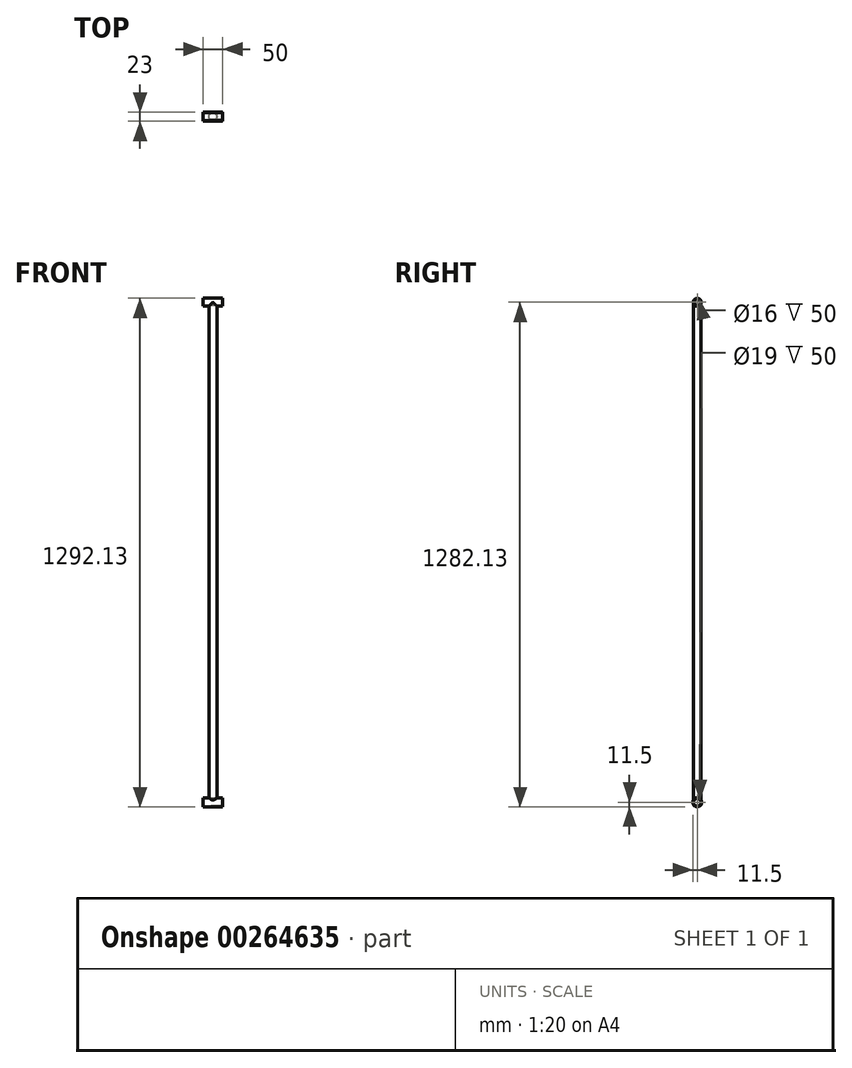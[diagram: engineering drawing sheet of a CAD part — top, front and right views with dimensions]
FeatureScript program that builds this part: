
annotation { "Feature Type Name" : "Feature", "Feature Type Description" : "" }
export const myFeature = defineFeature(function(context is Context, id is Id, definition is map)
    precondition{}
    {
        {
            var Q0;
            Q0=qCreatedBy(makeId("Front.planeOp"),FACE);
            var sketch = newSketch(context, id + "F0", { "sketchPlane" : qUnion([Q0])});
            skLineSegment(sketch, "E0", {"start": v(0, 0) * mm, "end": v(50, 0) * mm});
            skLineSegment(sketch, "E1", {"start": v(50, 23) * mm, "end": v(35, 23) * mm});
            skLineSegment(sketch, "E2", {"start": v(35, 23) * mm, "end": v(35, 1272.13) * mm});
            skLineSegment(sketch, "E3", {"start": v(35, 1272.13) * mm, "end": v(50, 1272.13) * mm});
            skLineSegment(sketch, "E4", {"start": v(50, 1292.13) * mm, "end": v(0, 1292.13) * mm});
            skLineSegment(sketch, "E5", {"start": v(0, 1272.13) * mm, "end": v(15, 1272.13) * mm});
            skLineSegment(sketch, "E6", {"start": v(15, 1272.13) * mm, "end": v(15, 23) * mm});
            skLineSegment(sketch, "E7", {"start": v(15, 23) * mm, "end": v(0, 23) * mm});
            skLineSegment(sketch, "E8", {"start": v(15, 23) * mm, "end": v(35, 23) * mm});
            skLineSegment(sketch, "E9", {"start": v(15, 1272.13) * mm, "end": v(35, 1272.13) * mm});
            skLineSegment(sketch, "E10", {"start": v(0, 1272.13) * mm, "end": v(0, 1274.13) * mm});
            skLineSegment(sketch, "E11", {"start": v(0, 1274.13) * mm, "end": v(0, 1290.13) * mm});
            skLineSegment(sketch, "E12", {"start": v(0, 1290.13) * mm, "end": v(0, 1292.13) * mm});
            skLineSegment(sketch, "E13", {"start": v(0, 1274.13) * mm, "end": v(50, 1274.13) * mm});
            skLineSegment(sketch, "E14", {"start": v(50, 1274.13) * mm, "end": v(50, 1272.13) * mm});
            skLineSegment(sketch, "E15", {"start": v(50, 1274.13) * mm, "end": v(50, 1290.13) * mm});
            skLineSegment(sketch, "E16", {"start": v(50, 1290.13) * mm, "end": v(50, 1292.13) * mm});
            skLineSegment(sketch, "E17", {"start": v(50, 1290.13) * mm, "end": v(0, 1290.13) * mm});
            skLineSegment(sketch, "E18", {"start": v(0, 0) * mm, "end": v(0, 2) * mm});
            skLineSegment(sketch, "E19", {"start": v(0, 2) * mm, "end": v(0, 21) * mm});
            skLineSegment(sketch, "E20", {"start": v(0, 21) * mm, "end": v(0, 23) * mm});
            skLineSegment(sketch, "E21", {"start": v(0, 21) * mm, "end": v(50, 21) * mm});
            skLineSegment(sketch, "E22", {"start": v(50, 21) * mm, "end": v(50, 23) * mm});
            skLineSegment(sketch, "E23", {"start": v(50, 21) * mm, "end": v(50, 2) * mm});
            skLineSegment(sketch, "E24", {"start": v(50, 2) * mm, "end": v(0, 2) * mm});
            skLineSegment(sketch, "E25", {"start": v(50, 2) * mm, "end": v(50, 0) * mm});
            skSolve(sketch);
        }
        {
            var Q0;
            Q0=makeQuery(id+"F0.imprint","IMPRINT",FACE,{"disambiguationData":[TD([[makeQuery(id+"F0.imprint","IMPRINT",EDGE,{"derivedFrom":sQuery(id+"F0.wireOp",EDGE,"E2")}),1.0]])]});
            var Q1;
            Q1=makeQuery(id+"F0.imprint","IMPRINT",FACE,{"disambiguationData":[TD([[makeQuery(id+"F0.imprint","IMPRINT",EDGE,{"derivedFrom":sQuery(id+"F0.wireOp",EDGE,"E3")}),1.0]])]});
            var Q2;
            Q2=makeQuery(id+"F0.imprint","IMPRINT",FACE,{"disambiguationData":[TD([[makeQuery(id+"F0.imprint","IMPRINT",EDGE,{"derivedFrom":sQuery(id+"F0.wireOp",EDGE,"E11")}),-1.0]])]});
            var Q3;
            Q3=makeQuery(id+"F0.imprint","IMPRINT",FACE,{"disambiguationData":[TD([[makeQuery(id+"F0.imprint","IMPRINT",EDGE,{"derivedFrom":sQuery(id+"F0.wireOp",EDGE,"E4")}),1.0]])]});
            extrude(context, id + "F1", {"entities" : qUnion([Q0, Q1, Q2, Q3]), "endBound" : BoundingType.SYMMETRIC, "depth" : 20 * mm});
        }
        {
            var Q0;
            Q0=makeQuery(id+"F0.imprint","IMPRINT",FACE,{"disambiguationData":[TD([[makeQuery(id+"F0.imprint","IMPRINT",EDGE,{"derivedFrom":sQuery(id+"F0.wireOp",EDGE,"E1")}),1.0]])]});
            var Q1;
            Q1=makeQuery(id+"F0.imprint","IMPRINT",FACE,{"disambiguationData":[TD([[makeQuery(id+"F0.imprint","IMPRINT",EDGE,{"derivedFrom":sQuery(id+"F0.wireOp",EDGE,"E19")}),-1.0]])]});
            var Q2;
            Q2=makeQuery(id+"F0.imprint","IMPRINT",FACE,{"disambiguationData":[TD([[makeQuery(id+"F0.imprint","IMPRINT",EDGE,{"derivedFrom":sQuery(id+"F0.wireOp",EDGE,"E0")}),1.0]])]});
            extrude(context, id + "F2", {"entities" : qUnion([Q0, Q1, Q2]), "operationType" : NewBodyOperationType.ADD, "endBound" : BoundingType.SYMMETRIC, "depth" : 23 * mm});
        }
        {
            var Q0;
            Q0=makeQuery(id+"F0.imprint","IMPRINT",FACE,{"disambiguationData":[TD([[makeQuery(id+"F0.imprint","IMPRINT",EDGE,{"derivedFrom":sQuery(id+"F0.wireOp",EDGE,"E19")}),-1.0]])]});
            extrude(context, id + "F3", {"entities" : qUnion([Q0]), "operationType" : NewBodyOperationType.REMOVE, "endBound" : BoundingType.SYMMETRIC, "oppositeDirection" : true, "depth" : 19 * mm});
        }
        {
            var Q0;
            Q0=makeQuery(id+"F0.imprint","IMPRINT",FACE,{"disambiguationData":[TD([[makeQuery(id+"F0.imprint","IMPRINT",EDGE,{"derivedFrom":sQuery(id+"F0.wireOp",EDGE,"E11")}),-1.0]])]});
            extrude(context, id + "F4", {"entities" : qUnion([Q0]), "operationType" : NewBodyOperationType.REMOVE, "endBound" : BoundingType.SYMMETRIC, "oppositeDirection" : true, "depth" : 16 * mm});
        }
        {
            var Q0;
            Q0=makeQuery(id+"F4.boolean.opBoolean","COPY",EDGE,{"derivedFrom":makeQuery(id+"F4.opExtrude","CAP_EDGE",EDGE,{"disambiguationData":[OSD([sQuery(id+"F0.wireOp",EDGE,"E17")])],"isStart":true})});
            var Q1;
            Q1=makeQuery(id+"F4.boolean.opBoolean","COPY",EDGE,{"derivedFrom":makeQuery(id+"F4.opExtrude","CAP_EDGE",EDGE,{"disambiguationData":[OSD([sQuery(id+"F0.wireOp",EDGE,"E13")])],"isStart":true})});
            var Q2;
            Q2=makeQuery(id+"F4.boolean.opBoolean","COPY",EDGE,{"derivedFrom":makeQuery(id+"F4.opExtrude","CAP_EDGE",EDGE,{"disambiguationData":[OSD([sQuery(id+"F0.wireOp",EDGE,"E13")])],"isStart":false})});
            var Q3;
            Q3=makeQuery(id+"F4.boolean.opBoolean","COPY",EDGE,{"derivedFrom":makeQuery(id+"F4.opExtrude","CAP_EDGE",EDGE,{"disambiguationData":[OSD([sQuery(id+"F0.wireOp",EDGE,"E17")])],"isStart":false})});
            fillet(context, id + "F5", {"entities" : qUnion([Q0, Q1, Q2, Q3]), "radius" : 8 * mm, "tangentPropagation" : true, "allowEdgeOverflow" : false});
        }
        {
            var Q0;
            Q0=makeQuery(id+"F3.boolean.opBoolean","COPY",EDGE,{"derivedFrom":makeQuery(id+"F3.opExtrude","CAP_EDGE",EDGE,{"disambiguationData":[OSD([sQuery(id+"F0.wireOp",EDGE,"E24")])],"isStart":false})});
            var Q1;
            Q1=makeQuery(id+"F3.boolean.opBoolean","COPY",EDGE,{"derivedFrom":makeQuery(id+"F3.opExtrude","CAP_EDGE",EDGE,{"disambiguationData":[OSD([sQuery(id+"F0.wireOp",EDGE,"E24")])],"isStart":true})});
            var Q2;
            Q2=makeQuery(id+"F3.boolean.opBoolean","COPY",EDGE,{"derivedFrom":makeQuery(id+"F3.opExtrude","CAP_EDGE",EDGE,{"disambiguationData":[OSD([sQuery(id+"F0.wireOp",EDGE,"E21")])],"isStart":true})});
            var Q3;
            Q3=makeQuery(id+"F3.boolean.opBoolean","COPY",EDGE,{"derivedFrom":makeQuery(id+"F3.opExtrude","CAP_EDGE",EDGE,{"disambiguationData":[OSD([sQuery(id+"F0.wireOp",EDGE,"E21")])],"isStart":false})});
            fillet(context, id + "F6", {"entities" : qUnion([Q0, Q1, Q2, Q3]), "radius" : 9.5 * mm, "tangentPropagation" : true, "allowEdgeOverflow" : false});
        }
        {
            var Q0;
            Q0=makeQuery(id+"F2.opExtrude","CAP_EDGE",EDGE,{"disambiguationData":[OSD([sQuery(id+"F0.wireOp",EDGE,"E1"),sQuery(id+"F0.wireOp",EDGE,"E7"),sQuery(id+"F0.wireOp",EDGE,"E8")])],"isStart":false});
            var Q1;
            Q1=makeQuery(id+"F2.opExtrude","CAP_EDGE",EDGE,{"disambiguationData":[OSD([sQuery(id+"F0.wireOp",EDGE,"E0")])],"isStart":false});
            var Q2;
            Q2=makeQuery(id+"F2.opExtrude","CAP_EDGE",EDGE,{"disambiguationData":[OSD([sQuery(id+"F0.wireOp",EDGE,"E0")])],"isStart":true});
            var Q3;
            Q3=makeQuery(id+"F2.opExtrude","CAP_EDGE",EDGE,{"disambiguationData":[OSD([sQuery(id+"F0.wireOp",EDGE,"E1"),sQuery(id+"F0.wireOp",EDGE,"E7"),sQuery(id+"F0.wireOp",EDGE,"E8")])],"isStart":true});
            fillet(context, id + "F7", {"entities" : qUnion([Q0, Q1, Q2, Q3]), "radius" : 11.5 * mm, "tangentPropagation" : true, "allowEdgeOverflow" : false});
        }
        {
            var Q0;
            Q0=makeQuery(id+"F1.opExtrude","CAP_EDGE",EDGE,{"disambiguationData":[OSD([sQuery(id+"F0.wireOp",EDGE,"E5")])],"isStart":false});
            var Q1;
            Q1=makeQuery(id+"F1.opExtrude","CAP_EDGE",EDGE,{"disambiguationData":[OSD([sQuery(id+"F0.wireOp",EDGE,"E4")])],"isStart":false});
            var Q2;
            Q2=makeQuery(id+"F1.opExtrude","CAP_EDGE",EDGE,{"disambiguationData":[OSD([sQuery(id+"F0.wireOp",EDGE,"E3")])],"isStart":false});
            var Q3;
            Q3=makeQuery(id+"F1.opExtrude","CAP_EDGE",EDGE,{"disambiguationData":[OSD([sQuery(id+"F0.wireOp",EDGE,"E2")])],"isStart":false});
            var Q4;
            Q4=makeQuery(id+"F1.opExtrude","CAP_EDGE",EDGE,{"disambiguationData":[OSD([sQuery(id+"F0.wireOp",EDGE,"E6")])],"isStart":false});
            var Q5;
            Q5=makeQuery(id+"F1.opExtrude","CAP_EDGE",EDGE,{"disambiguationData":[OSD([sQuery(id+"F0.wireOp",EDGE,"E2")])],"isStart":true});
            var Q6;
            Q6=makeQuery(id+"F1.opExtrude","CAP_EDGE",EDGE,{"disambiguationData":[OSD([sQuery(id+"F0.wireOp",EDGE,"E3")])],"isStart":true});
            var Q7;
            Q7=makeQuery(id+"F1.opExtrude","CAP_EDGE",EDGE,{"disambiguationData":[OSD([sQuery(id+"F0.wireOp",EDGE,"E4")])],"isStart":true});
            var Q8;
            Q8=makeQuery(id+"F1.opExtrude","CAP_EDGE",EDGE,{"disambiguationData":[OSD([sQuery(id+"F0.wireOp",EDGE,"E6")])],"isStart":true});
            var Q9;
            Q9=makeQuery(id+"F1.opExtrude","CAP_EDGE",EDGE,{"disambiguationData":[OSD([sQuery(id+"F0.wireOp",EDGE,"E5")])],"isStart":true});
            fillet(context, id + "F8", {"entities" : qUnion([Q0, Q1, Q2, Q3, Q4, Q5, Q6, Q7, Q8, Q9]), "radius" : 10 * mm, "tangentPropagation" : true, "allowEdgeOverflow" : false});
        }
    });
